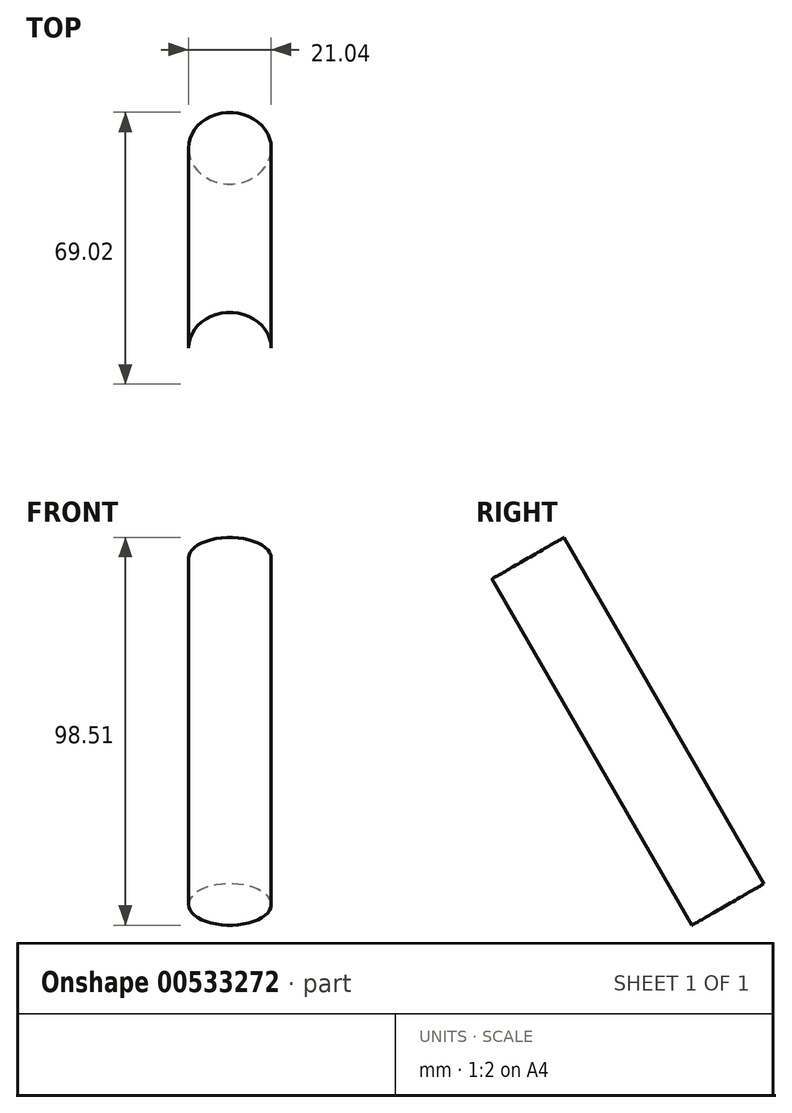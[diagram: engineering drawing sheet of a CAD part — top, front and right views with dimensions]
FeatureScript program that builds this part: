
annotation { "Feature Type Name" : "Feature", "Feature Type Description" : "" }
export const myFeature = defineFeature(function(context is Context, id is Id, definition is map)
    precondition{}
    {
        {
            var Q0;
            Q0=qCreatedBy(makeId("Top.planeOp"),FACE);
            var sketch = newSketch(context, id + "F0", { "sketchPlane" : qUnion([Q0])});
            skCircle(sketch, "E0", {"center": v(0, 0) * mm, "radius": 10.52 * mm});
            skLineSegment(sketch, "E1", {"start": v(-10.52, 0) * mm, "end": v(10.52, 0) * mm});
            skSolve(sketch);
        }
        {
            var Q0;
            Q0=makeQuery(id+"F0.imprint","IMPRINT",FACE,{"disambiguationData":[TD([[makeQuery(id+"F0.imprint","IMPRINT",EDGE,{"derivedFrom":sQuery(id+"F0.wireOp",EDGE,"E0")}),1.0]])]});
            extrude(context, id + "F1", {"entities" : qUnion([Q0]), "depth" : 101.6 * mm, "offsetDistance" : 25.4 * mm});
        }
        {
            var Q0;
            Q0=makeQuery(id+"F1.opExtrude","SWEPT_BODY",BODY,{"disambiguationData":[OSD([sQuery(id+"F0.wireOp",EDGE,"E0")])]});
            var Q1;
            Q1=sQuery(id+"F0.wireOp",EDGE,"E1");
            transform(context, id + "F2", {"entities" : qUnion([Q0]), "transformType" : TransformType.ROTATION, "transformAxis" : qUnion([Q1]), "angle" : 30 * degree, "makeCopy" : false});
        }
    });
